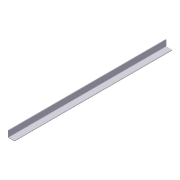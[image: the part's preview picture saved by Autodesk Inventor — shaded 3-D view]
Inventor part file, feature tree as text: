
AUTODESK INVENTOR PART (.ipt)
format: ipt  version: 2012 (Build 160160000, 160)  size: 72,704 bytes
history: native  units: in
note: dims shown in document units (in); Inventor stores cm internally (conversion verified against a paired STEP export)
features: extrude x1, sketch x1
ambient origin geometry x8: Origin, YZ Plane, XZ Plane, XY Plane, X Axis, Y Axis, Z Axis, Center Point
bodies: Solid1 (feature_tree)
feature tree (2):
  extrude  "Extrusion1"  Depth=0.24in
  sketch  "Sketch1"  dims[d0=3.0in d1=0.24in d2=0.25in d3=0.25in d4=72.0in d5=0.0in]
